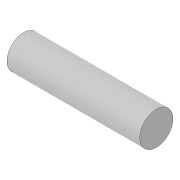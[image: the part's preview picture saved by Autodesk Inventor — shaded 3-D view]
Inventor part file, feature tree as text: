
AUTODESK INVENTOR PART (.ipt)
format: ipt  version: 2019 (Build 230136000, 136)  size: 71,680 bytes
history: native  units: in
note: dims shown in document units (in); Inventor stores cm internally (conversion verified against a paired STEP export)
features: extrude x1, sketch x1
ambient origin geometry x8: Origin, YZ Plane, XZ Plane, XY Plane, X Axis, Y Axis, Z Axis, Center Point
bodies: Solid1 (feature_tree)
feature tree (2):
  extrude  "Extrusion1"  Depth=2.0in TaperAngle=0.0deg
  sketch  "Sketch1"  dims[d0=0.5in d1=2.0in d2=0.0in]
